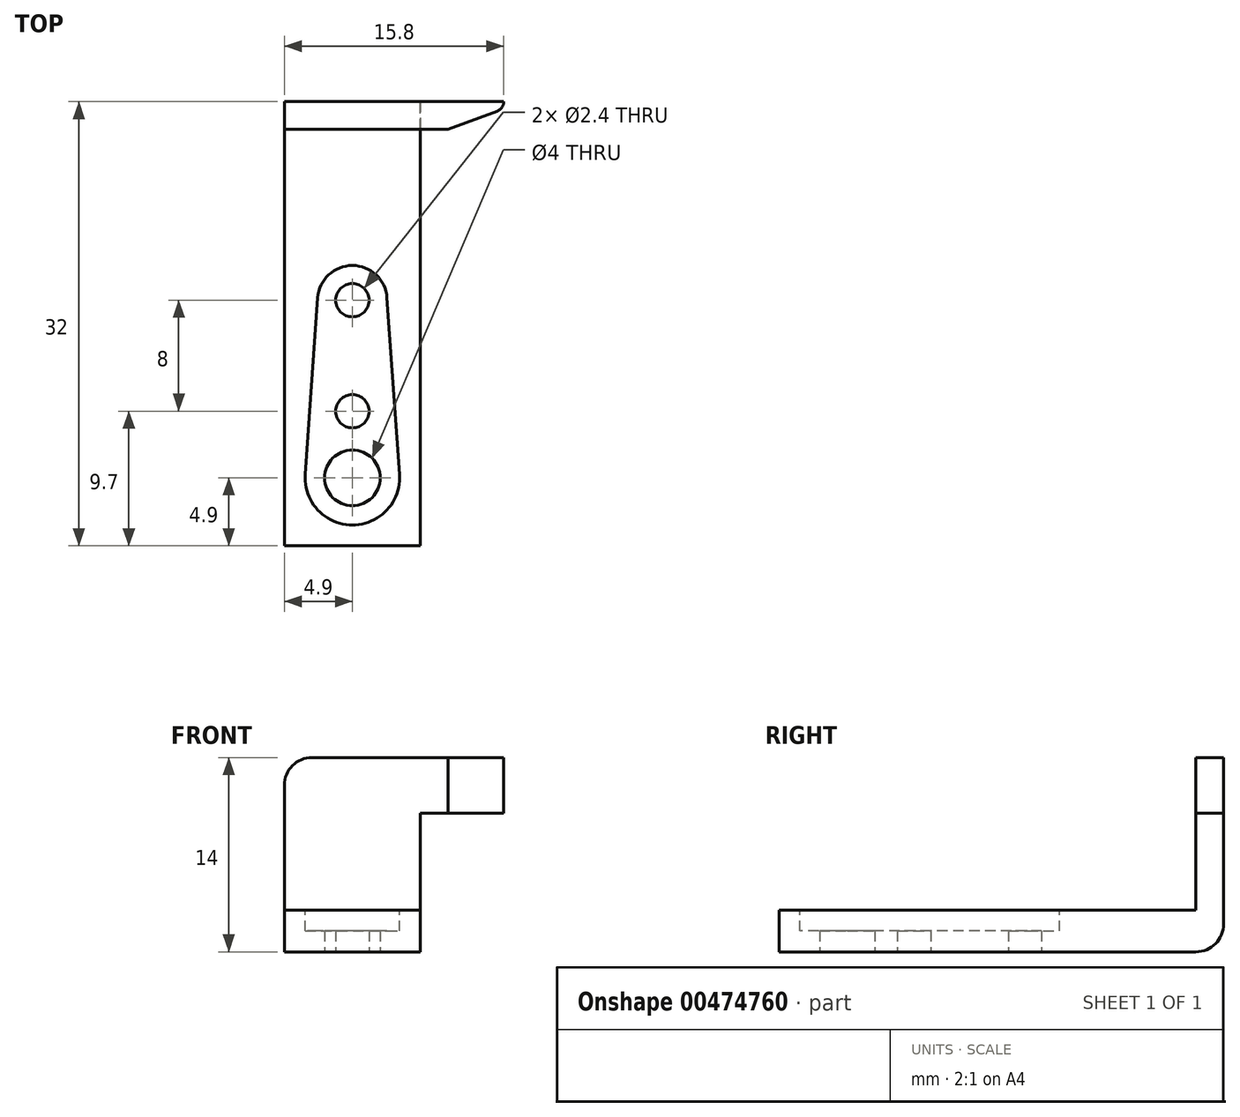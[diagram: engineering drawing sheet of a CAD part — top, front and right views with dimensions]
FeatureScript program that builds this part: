
annotation { "Feature Type Name" : "Feature", "Feature Type Description" : "" }
export const myFeature = defineFeature(function(context is Context, id is Id, definition is map)
    precondition{}
    {
        {
            var Q0;
            Q0=qCreatedBy(makeId("Top.planeOp"),FACE);
            var sketch = newSketch(context, id + "F0", { "sketchPlane" : qUnion([Q0])});
            skArc(sketch, "E0", {"start": v(-2.9, 0.2) * mm, "mid": v(0, -2.9) * mm, "end": v(2.9, 0.2) * mm, "construction": true});
            skArc(sketch, "E1", {"start": v(2, 12.94) * mm, "mid": v(0, 14.8) * mm, "end": v(-2, 12.94) * mm, "construction": true});
            skLineSegment(sketch, "E2", {"start": v(-2, 12.94) * mm, "end": v(-2.9, 0.2) * mm, "construction": true});
            skLineSegment(sketch, "E3", {"start": v(2, 12.94) * mm, "end": v(2.9, 0.2) * mm, "construction": true});
            skLineSegment(sketch, "E4.bottom", {"start": v(-4.9, -4.9) * mm, "end": v(4.9, -4.9) * mm});
            skLineSegment(sketch, "E4.top", {"start": v(-4.9, 27.1) * mm, "end": v(4.9, 27.1) * mm});
            skLineSegment(sketch, "E4.left", {"start": v(-4.9, -4.9) * mm, "end": v(-4.9, 27.1) * mm});
            skLineSegment(sketch, "E4.right", {"start": v(4.9, -4.9) * mm, "end": v(4.9, 27.1) * mm});
            skCircle(sketch, "E5", {"center": v(0, 12.8) * mm, "radius": 1.2 * mm});
            skCircle(sketch, "E6", {"center": v(0, 4.8) * mm, "radius": 1.2 * mm});
            skCircle(sketch, "E7", {"center": v(0, 0) * mm, "radius": 2 * mm});
            skSolve(sketch);
        }
        {
            var Q0;
            Q0 = qSketchRegion(id + "F0", true);
            extrude(context, id + "F1", {"entities" : qUnion([Q0]), "depth" : 3 * mm, "offsetDistance" : 25 * mm});
        }
        {
            var Q0;
            Q0=makeQuery(id+"F1.opExtrude","CAP_FACE",FACE,{"disambiguationData":[OSD([sQuery(id+"F0.wireOp",EDGE,"E4.bottom"),sQuery(id+"F0.wireOp",EDGE,"E4.top"),sQuery(id+"F0.wireOp",EDGE,"E4.left"),sQuery(id+"F0.wireOp",EDGE,"E4.right"),sQuery(id+"F0.wireOp",EDGE,"E5"),sQuery(id+"F0.wireOp",EDGE,"E6"),sQuery(id+"F0.wireOp",EDGE,"E7")])],"isStart":false});
            var sketch = newSketch(context, id + "F2", { "sketchPlane" : qUnion([Q0])});
            skArc(sketch, "E8", {"start": v(-3.4, 0.24) * mm, "mid": v(0, -3.4) * mm, "end": v(3.4, 0.24) * mm});
            skArc(sketch, "E9", {"start": v(2.5, 12.98) * mm, "mid": v(0, 15.3) * mm, "end": v(-2.5, 12.98) * mm});
            skLineSegment(sketch, "E10", {"start": v(-2.5, 12.98) * mm, "end": v(-3.4, 0.24) * mm});
            skLineSegment(sketch, "E11", {"start": v(2.5, 12.98) * mm, "end": v(3.4, 0.24) * mm});
            skSolve(sketch);
        }
        {
            var Q0;
            Q0 = qSketchRegion(id + "F2", true);
            extrude(context, id + "F3", {"entities" : qUnion([Q0]), "operationType" : NewBodyOperationType.REMOVE, "oppositeDirection" : true, "depth" : 1.5 * mm, "offsetDistance" : 25 * mm});
        }
        {
            var Q0;
            Q0=makeQuery(id+"F1.opExtrude","CAP_FACE",FACE,{"disambiguationData":[OSD([sQuery(id+"F0.wireOp",EDGE,"E4.bottom"),sQuery(id+"F0.wireOp",EDGE,"E4.top"),sQuery(id+"F0.wireOp",EDGE,"E4.left"),sQuery(id+"F0.wireOp",EDGE,"E4.right"),sQuery(id+"F0.wireOp",EDGE,"E5"),sQuery(id+"F0.wireOp",EDGE,"E6"),sQuery(id+"F0.wireOp",EDGE,"E7")])],"isStart":false});
            var sketch = newSketch(context, id + "F4", { "sketchPlane" : qUnion([Q0])});
            skLineSegment(sketch, "E12.bottom", {"start": v(-4.9, 27.1) * mm, "end": v(4.9, 27.1) * mm});
            skLineSegment(sketch, "E12.top", {"start": v(-4.9, 25.1) * mm, "end": v(4.9, 25.1) * mm});
            skLineSegment(sketch, "E12.left", {"start": v(-4.9, 27.1) * mm, "end": v(-4.9, 25.1) * mm});
            skLineSegment(sketch, "E12.right", {"start": v(4.9, 27.1) * mm, "end": v(4.9, 25.1) * mm});
            skSolve(sketch);
        }
        {
            var Q0;
            Q0 = qSketchRegion(id + "F4", true);
            extrude(context, id + "F5", {"entities" : qUnion([Q0]), "operationType" : NewBodyOperationType.ADD, "depth" : 11 * mm, "offsetDistance" : 25 * mm});
        }
        {
            var Q0;
            Q0=makeQuery(id+"F5.boolean.opBoolean","MERGE",FACE,{"derivedFrom":[makeQuery(id+"F1.opExtrude","SWEPT_FACE",FACE,{"disambiguationData":[OSD([sQuery(id+"F0.wireOp",EDGE,"E4.right")])]}),makeQuery(id+"F5.opExtrude","SWEPT_FACE",FACE,{"disambiguationData":[OSD([sQuery(id+"F4.wireOp",EDGE,"E12.right")])]})]});
            var sketch = newSketch(context, id + "F6", { "sketchPlane" : qUnion([Q0])});
            skLineSegment(sketch, "E13.bottom", {"start": v(25.1, 14) * mm, "end": v(27.1, 14) * mm});
            skLineSegment(sketch, "E13.top", {"start": v(25.1, 10) * mm, "end": v(27.1, 10) * mm});
            skLineSegment(sketch, "E13.left", {"start": v(25.1, 14) * mm, "end": v(25.1, 10) * mm});
            skLineSegment(sketch, "E13.right", {"start": v(27.1, 14) * mm, "end": v(27.1, 10) * mm});
            skSolve(sketch);
        }
        {
            var Q0;
            Q0 = qSketchRegion(id + "F6", true);
            extrude(context, id + "F7", {"entities" : qUnion([Q0]), "operationType" : NewBodyOperationType.ADD, "depth" : 6 * mm, "offsetDistance" : 25 * mm});
        }
        {
            var Q0;
            Q0=makeQuery(id+"F7.opExtrude","CAP_EDGE",EDGE,{"disambiguationData":[OSD([sQuery(id+"F6.wireOp",EDGE,"E13.top")])],"isStart":true});
            var Q1;
            Q1=makeQuery(id+"F5.opExtrude","CAP_EDGE",EDGE,{"disambiguationData":[OSD([sQuery(id+"F4.wireOp",EDGE,"E12.left")])],"isStart":false});
            var Q2;
            Q2=makeQuery(id+"F5.opExtrude","CAP_EDGE",EDGE,{"disambiguationData":[OSD([sQuery(id+"F4.wireOp",EDGE,"E12.top")])],"isStart":true});
            var Q3;
            Q3=makeQuery(id+"F1.opExtrude","CAP_EDGE",EDGE,{"disambiguationData":[OSD([sQuery(id+"F0.wireOp",EDGE,"E4.top")])],"isStart":true});
            fillet(context, id + "F8", {"entities" : qUnion([Q0, Q1, Q2, Q3]), "radius" : 2 * mm, "tangentPropagation" : true, "allowEdgeOverflow" : false});
        }
        {
            var Q0;
            Q0=makeQuery(id+"F7.opExtrude","SWEPT_FACE",FACE,{"disambiguationData":[OSD([sQuery(id+"F6.wireOp",EDGE,"E13.top")])]});
            var sketch = newSketch(context, id + "F9", { "sketchPlane" : qUnion([Q0])});
            skLineSegment(sketch, "E14", {"start": v(6.9, -25.1) * mm, "end": v(10.43, -26.42) * mm});
            skLineSegment(sketch, "E15", {"start": v(10.9, -26.6) * mm, "end": v(10.9, -25.1) * mm});
            skLineSegment(sketch, "E16", {"start": v(10.9, -25.1) * mm, "end": v(6.9, -25.1) * mm});
            skArc(sketch, "E17", {"start": v(10.9, -27.1) * mm, "mid": v(10.77, -26.69) * mm, "end": v(10.43, -26.42) * mm});
            skLineSegment(sketch, "E18", {"start": v(10.9, -26.6) * mm, "end": v(10.9, -27.1) * mm});
            skSolve(sketch);
        }
        {
            var Q0;
            Q0 = qSketchRegion(id + "F9", true);
            extrude(context, id + "F10", {"entities" : qUnion([Q0]), "operationType" : NewBodyOperationType.REMOVE, "endBound" : BoundingType.UP_TO_NEXT, "oppositeDirection" : true, "depth" : 25 * mm, "offsetDistance" : 25 * mm});
        }
    });
